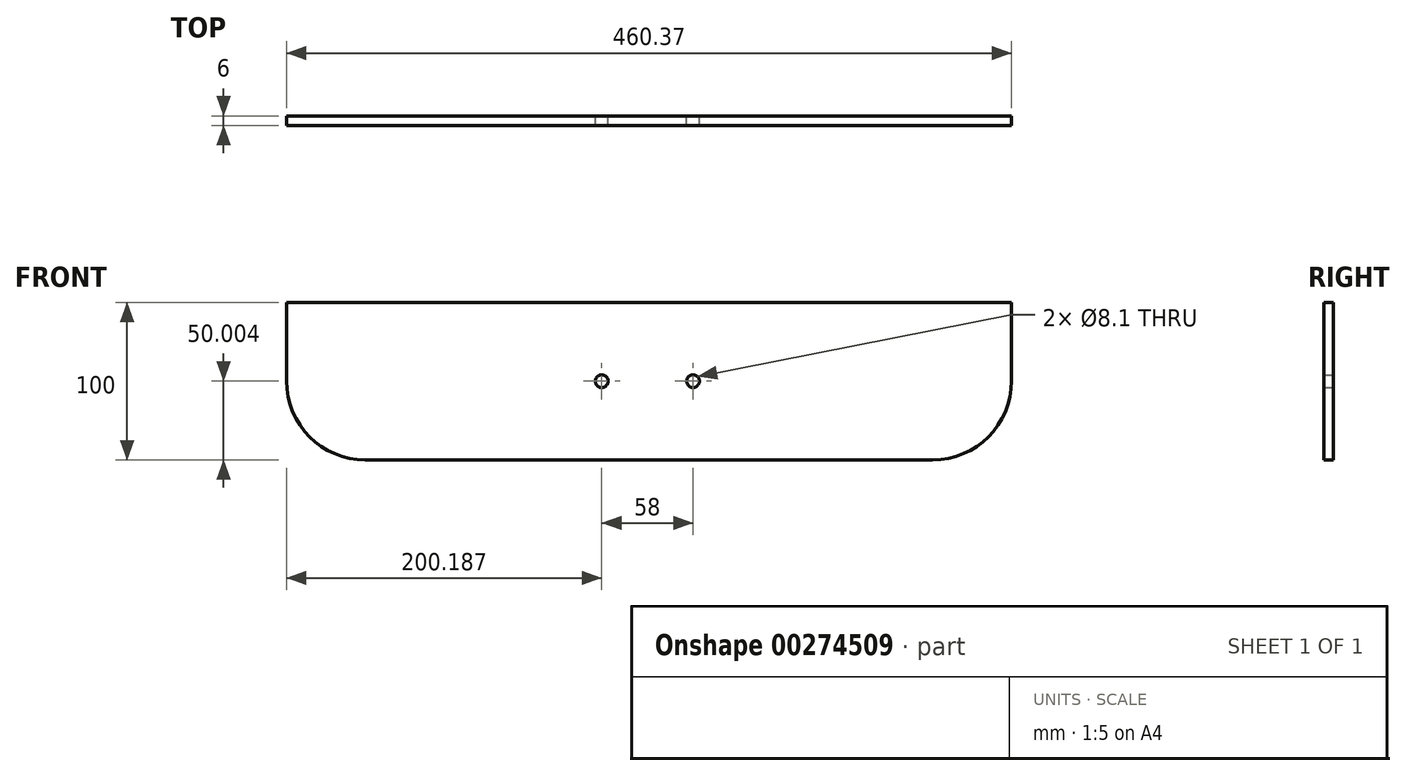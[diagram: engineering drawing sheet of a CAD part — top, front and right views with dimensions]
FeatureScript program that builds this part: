
annotation { "Feature Type Name" : "Feature", "Feature Type Description" : "" }
export const myFeature = defineFeature(function(context is Context, id is Id, definition is map)
    precondition{}
    {
        {
            var Q0;
            Q0=qCreatedBy(makeId("Front.planeOp"),FACE);
            var sketch = newSketch(context, id + "F0", { "sketchPlane" : qUnion([Q0])});
            skLineSegment(sketch, "E0.bottom", {"start": v(-230.47, -26.68) * mm, "end": v(229.9, -26.68) * mm});
            skLineSegment(sketch, "E0.top", {"start": v(-180.47, -126.68) * mm, "end": v(179.9, -126.68) * mm});
            skLineSegment(sketch, "E0.left", {"start": v(-230.47, -26.68) * mm, "end": v(-230.47, -76.68) * mm});
            skLineSegment(sketch, "E0.right", {"start": v(229.9, -26.68) * mm, "end": v(229.9, -76.68) * mm});
            skPoint(sketch, "E1.visualSharp", {"position": v(-230.47, -126.68) * mm});
            skArc(sketch, "E1.filletArc", {"start": v(-230.47, -76.68) * mm, "mid": v(-215.83, -112.03) * mm, "end": v(-180.47, -126.68) * mm});
            skPoint(sketch, "E2.visualSharp", {"position": v(229.9, -126.68) * mm});
            skArc(sketch, "E2.filletArc", {"start": v(179.9, -126.68) * mm, "mid": v(215.26, -112.03) * mm, "end": v(229.9, -76.68) * mm});
            skPoint(sketch, "E3", {"position": v(-30.28, -76.68) * mm});
            skPoint(sketch, "E4", {"position": v(27.72, -76.68) * mm});
            skSolve(sketch);
        }
        {
            var Q0;
            Q0 = qSketchRegion(id + "F0", true);
            extrude(context, id + "F1", {"entities" : qUnion([Q0]), "depth" : 6 * mm});
        }
        {
            var Q0;
            Q0=sQuery(id+"F0.wireOp",VERTEX,"E3");
            var Q1;
            Q1=sQuery(id+"F0.wireOp",VERTEX,"E4");
            var Q2;
            Q2=makeQuery(id+"F1.opExtrude","SWEPT_BODY",BODY,{"disambiguationData":[OSD([sQuery(id+"F0.wireOp",EDGE,"E0.bottom"),sQuery(id+"F0.wireOp",EDGE,"E0.top"),sQuery(id+"F0.wireOp",EDGE,"E0.left"),sQuery(id+"F0.wireOp",EDGE,"E0.right"),sQuery(id+"F0.wireOp",EDGE,"E1.filletArc"),sQuery(id+"F0.wireOp",EDGE,"E2.filletArc")])]});
            hole(context, id + "F2", {"style" : HoleStyle.SIMPLE, "endStyle" : HoleEndStyle.THROUGH, "oppositeDirection" : true, "standardTappedOrClearance" : lookupTablePath({ "standard" : "ISO", "size" : "8.1", "type" : "Drilled" }), "standardBlindInLast" : lookupTablePath({ "standard" : "ISO", "size" : "8.1", "type" : "Drilled" }), "holeDiameter" : 8.1 * mm, "tappedDepth" : 12 * mm, "tapClearance" : 3, "locations" : qUnion([Q0, Q1]), "scope" : qUnion([Q2])});
        }
    });
